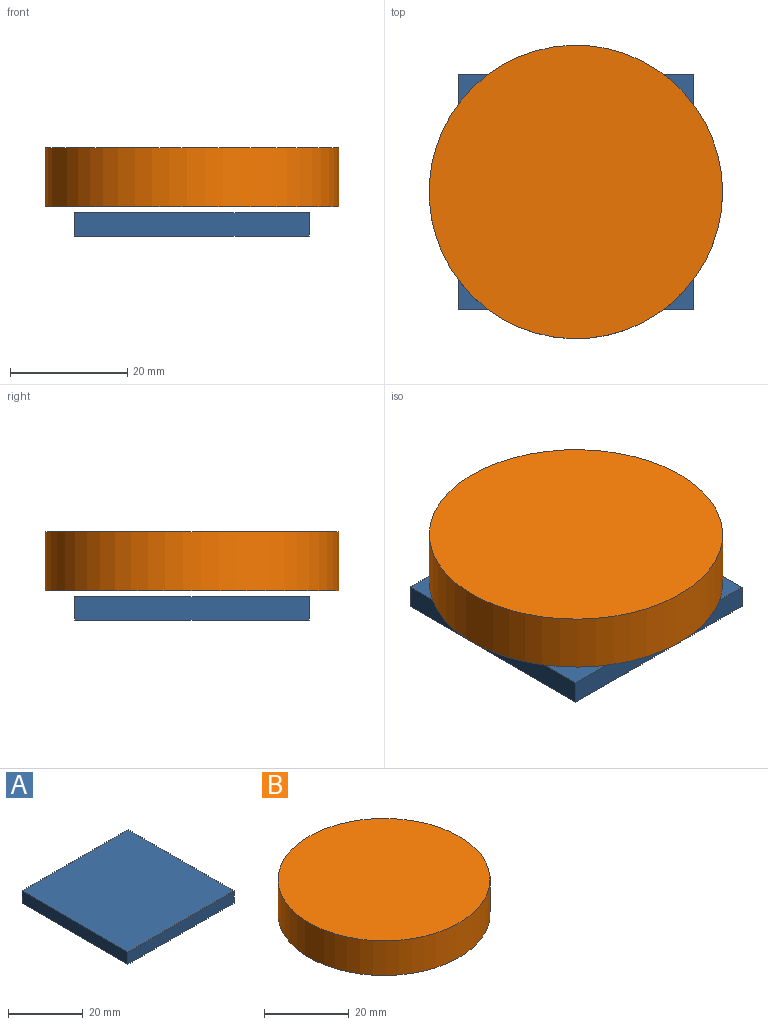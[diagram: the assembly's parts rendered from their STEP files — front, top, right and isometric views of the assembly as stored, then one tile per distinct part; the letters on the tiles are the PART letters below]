
ASSEMBLY  parts=2 mates=1
PART A: 6 faces, bbox 40x40x4 mm
  f0: plane 40x4mm, normal (0,-1,0), area 160mm2, adj f1,f3,f4,f5
  f1: plane 40x4mm, normal (1,0,0), area 160mm2, adj f0,f2,f4,f5
  f2: plane 40x4mm, normal (0,1,0), area 160mm2, adj f1,f3,f4,f5
  f3: plane 40x4mm, normal (-1,0,0), area 160mm2, adj f0,f2,f4,f5
  f4: plane 40x40mm, normal (0,0,-1), area 1600mm2, adj f0,f1,f2,f3
  f5: plane 40x40mm, normal (0,0,1), area 1600mm2, adj f0,f1,f2,f3
PART B: 3 faces, bbox 50x50x10 mm
  f0: cylinder r=25mm len=50mm, axis (0,0,-1), area 1570.8mm2, adj f1,f2
  f1: plane 50x50mm, normal (0,0,1), area 1963.5mm2, adj f0
  f2: plane 50x50mm, normal (0,0,-1), area 1963.5mm2, adj f0
PLACE A t=(0,0,5)mm
PLACE B t=(0,0,5)mm
MATE slider B.f0 <-> A.f5  axis (0,0,1) through (0,0,15)mm
